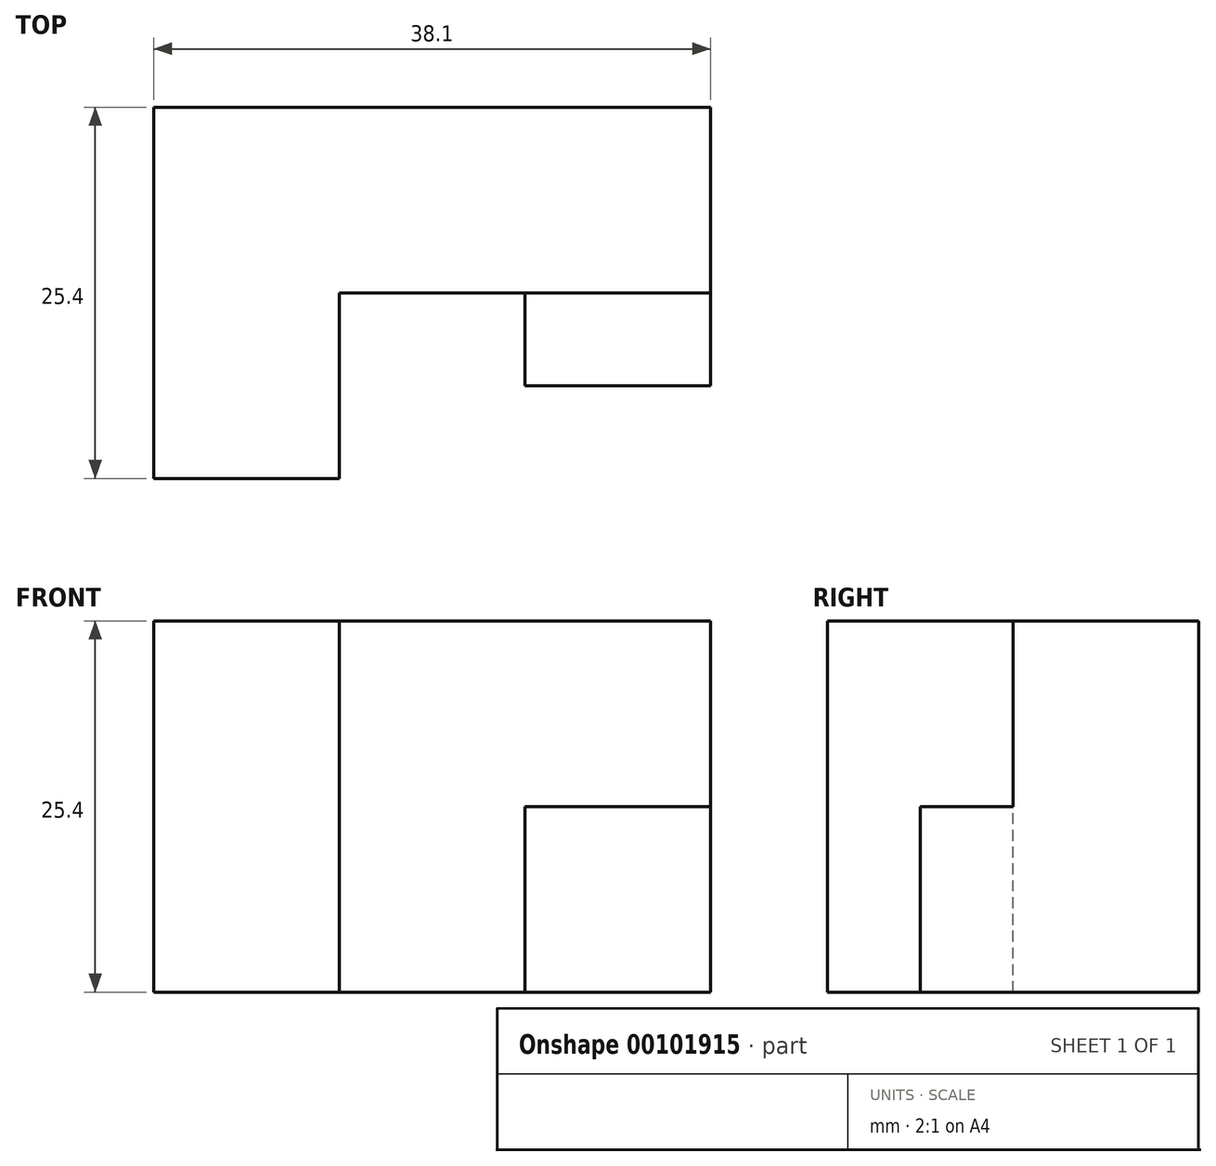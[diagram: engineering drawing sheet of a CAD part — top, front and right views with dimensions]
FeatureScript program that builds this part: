
annotation { "Feature Type Name" : "Feature", "Feature Type Description" : "" }
export const myFeature = defineFeature(function(context is Context, id is Id, definition is map)
    precondition{}
    {
        {
            var Q0;
            Q0=qCreatedBy(makeId("Top.planeOp"),FACE);
            var sketch = newSketch(context, id + "F0", { "sketchPlane" : qUnion([Q0])});
            skLineSegment(sketch, "E0", {"start": v(0, 0) * mm, "end": v(0, 25.4) * mm});
            skLineSegment(sketch, "E1", {"start": v(0, 25.4) * mm, "end": v(38.1, 25.4) * mm});
            skLineSegment(sketch, "E2", {"start": v(38.1, 25.4) * mm, "end": v(38.1, 12.7) * mm});
            skLineSegment(sketch, "E3", {"start": v(38.1, 12.7) * mm, "end": v(12.7, 12.7) * mm});
            skLineSegment(sketch, "E4", {"start": v(12.7, 12.7) * mm, "end": v(12.7, 0) * mm});
            skLineSegment(sketch, "E5", {"start": v(12.7, 0) * mm, "end": v(0, 0) * mm});
            skSolve(sketch);
        }
        {
            var Q0;
            Q0 = qSketchRegion(id + "F0", true);
            extrude(context, id + "F1", {"entities" : qUnion([Q0]), "depth" : 25.4 * mm});
        }
        {
            var Q0;
            Q0=makeQuery(id+"F1.opExtrude","SWEPT_FACE",FACE,{"disambiguationData":[OSD([sQuery(id+"F0.wireOp",EDGE,"E3")])]});
            var sketch = newSketch(context, id + "F2", { "sketchPlane" : qUnion([Q0])});
            skLineSegment(sketch, "E6.bottom", {"start": v(38.1, 0) * mm, "end": v(25.4, 0) * mm});
            skLineSegment(sketch, "E6.top", {"start": v(38.1, 12.7) * mm, "end": v(25.4, 12.7) * mm});
            skLineSegment(sketch, "E6.left", {"start": v(38.1, 0) * mm, "end": v(38.1, 12.7) * mm});
            skLineSegment(sketch, "E6.right", {"start": v(25.4, 0) * mm, "end": v(25.4, 12.7) * mm});
            skSolve(sketch);
        }
        {
            var Q0;
            Q0 = qSketchRegion(id + "F2", true);
            extrude(context, id + "F3", {"entities" : qUnion([Q0]), "operationType" : NewBodyOperationType.ADD, "depth" : 6.35 * mm});
        }
    });
